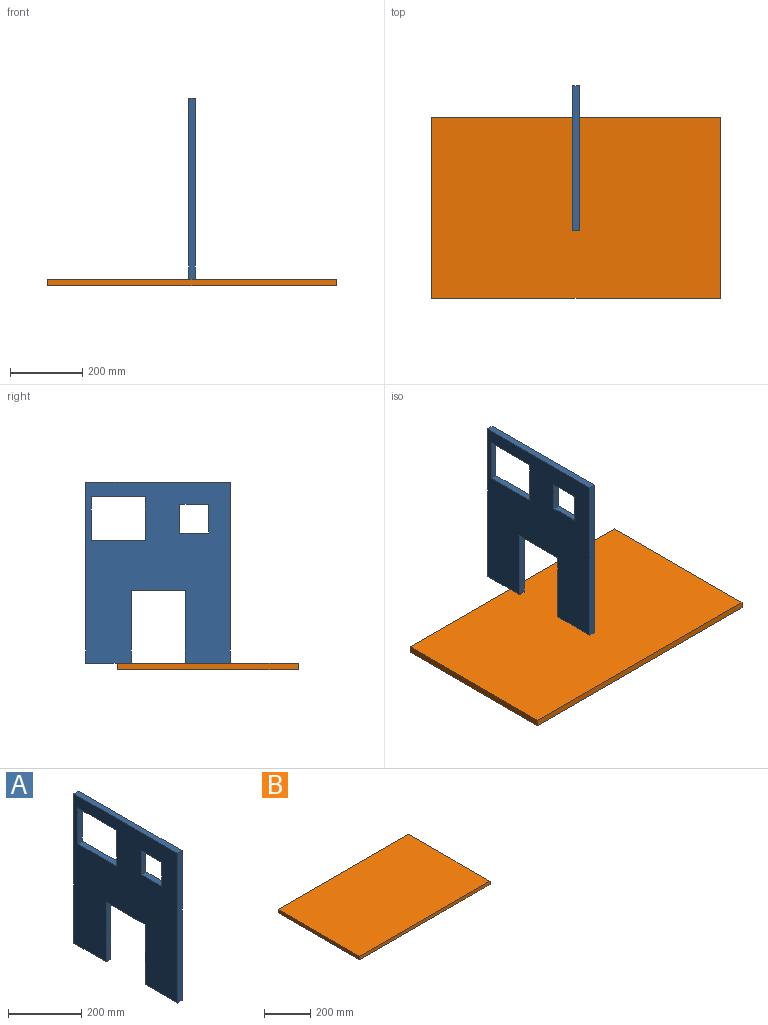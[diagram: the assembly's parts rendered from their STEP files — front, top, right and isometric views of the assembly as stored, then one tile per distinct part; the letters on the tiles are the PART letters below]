
ASSEMBLY  parts=2 mates=1
PART A: 18 faces, bbox 18x400x500 mm
  f0: plane 200x18mm, normal (0,-1,0), area 3600mm2, adj f1,f15,f16,f17
  f1: plane 125x18mm, normal (0,0,-1), area 2250mm2, adj f0,f2,f16,f17
  f2: plane 500x18mm, normal (0,1,0), area 9000mm2, adj f1,f3,f16,f17
  f3: plane 400x18mm, normal (0,0,1), area 7200mm2, adj f2,f4,f16,f17
  f4: plane 500x18mm, normal (0,-1,0), area 9000mm2, adj f3,f5,f16,f17
  f5: plane 125x18mm, normal (0,0,-1), area 2250mm2, adj f4,f6,f16,f17
  f6: plane 200x18mm, normal (0,1,0), area 3600mm2, adj f5,f15,f16,f17
  f7: plane 120x18mm, normal (0,-1,0), area 2160mm2, adj f8,f13,f16,f17
  f8: plane 150x18mm, normal (0,0,1), area 2700mm2, adj f7,f9,f16,f17
  f9: plane 120x18mm, normal (0,1,0), area 2160mm2, adj f8,f13,f16,f17
  f10: plane 80x18mm, normal (0,-1,0), area 1440mm2, adj f11,f14,f16,f17
  f11: plane 80x18mm, normal (0,0,1), area 1440mm2, adj f10,f12,f16,f17
  f12: plane 80x18mm, normal (0,1,0), area 1440mm2, adj f11,f14,f16,f17
  f13: plane 150x18mm, normal (0,0,-1), area 2700mm2, adj f7,f9,f16,f17
  f14: plane 80x18mm, normal (0,0,-1), area 1440mm2, adj f10,f12,f16,f17
  f15: plane 150x18mm, normal (0,0,-1), area 2700mm2, adj f0,f6,f16,f17
  f16: plane 500x400mm, normal (1,0,0), area 145600mm2, adj f0,f1,f2,f3,f4,f5,f6,f7
  f17: plane 500x400mm, normal (-1,0,0), area 145600mm2, adj f0,f1,f2,f3,f4,f5,f6,f7
PART B: 6 faces, bbox 800x500x18 mm
  f0: plane 800x18mm, normal (0,1,0), area 14400mm2, adj f1,f3,f4,f5
  f1: plane 500x18mm, normal (-1,0,0), area 9000mm2, adj f0,f2,f4,f5
  f2: plane 800x18mm, normal (0,-1,0), area 14400mm2, adj f1,f3,f4,f5
  f3: plane 500x18mm, normal (1,0,0), area 9000mm2, adj f0,f2,f4,f5
  f4: plane 800x500mm, normal (0,0,1), area 400000mm2, adj f0,f1,f2,f3
  f5: plane 800x500mm, normal (0,0,-1), area 400000mm2, adj f0,f1,f2,f3
PLACE A t=(20.4,134.85,237.36)mm
PLACE B t=(20.4,-2.65,-21.64)mm
MATE fastened A.f5 <-> B.f4  axis (0,0,-1) through (20.4,-2.65,-12.64)mm
